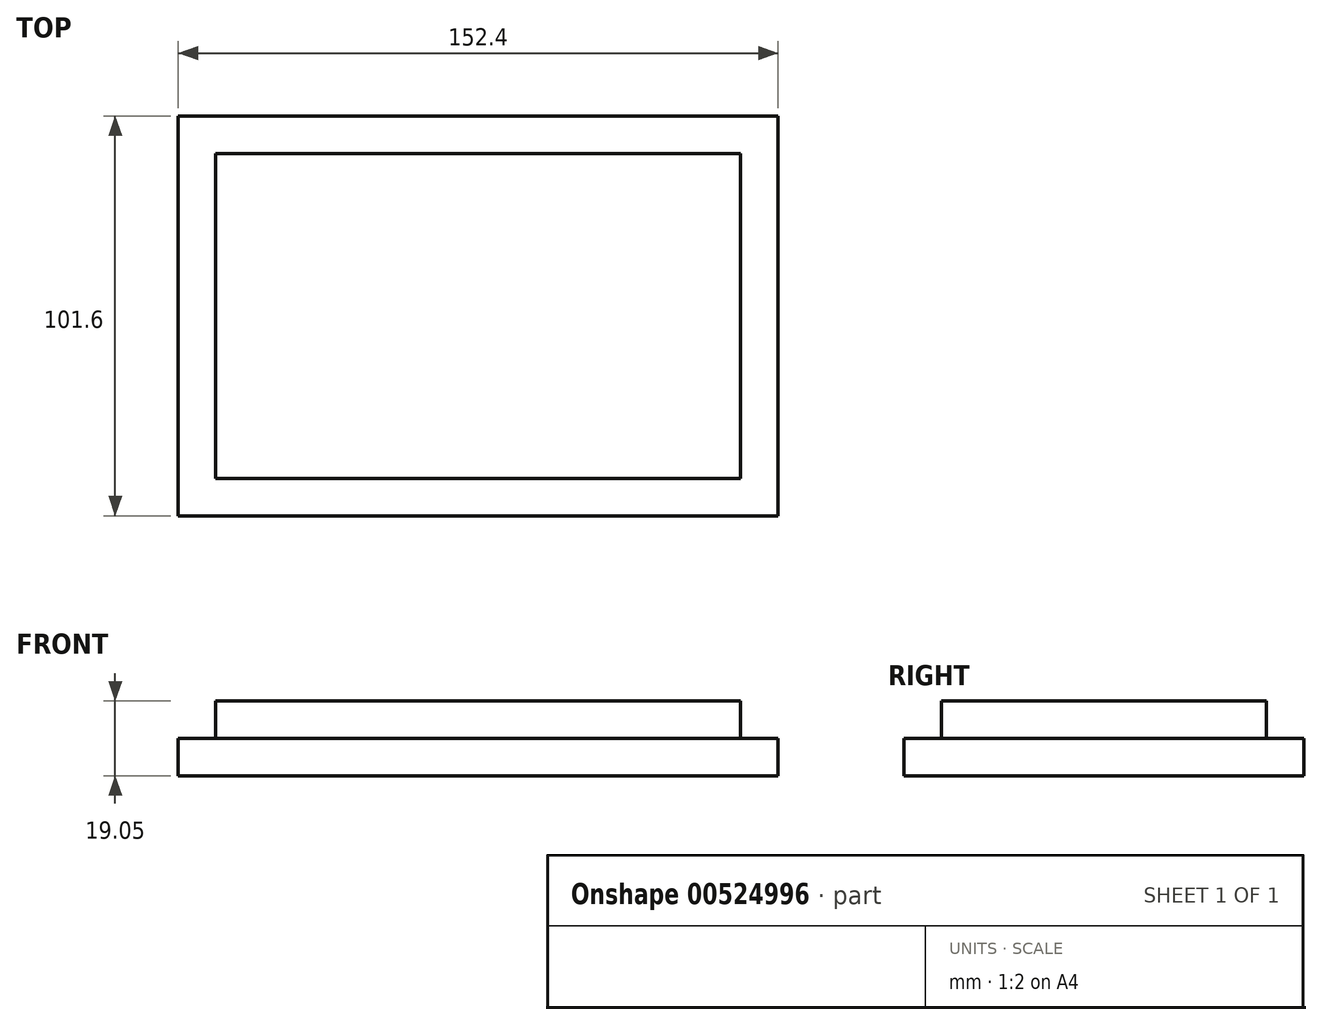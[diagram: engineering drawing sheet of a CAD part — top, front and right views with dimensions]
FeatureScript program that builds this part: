
annotation { "Feature Type Name" : "Feature", "Feature Type Description" : "" }
export const myFeature = defineFeature(function(context is Context, id is Id, definition is map)
    precondition{}
    {
        {
            var Q0;
            Q0=qCreatedBy(makeId("Top.planeOp"),FACE);
            var sketch = newSketch(context, id + "F0", { "sketchPlane" : qUnion([Q0])});
            skLineSegment(sketch, "E0.bottom", {"start": v(76.2, -50.8) * mm, "end": v(-76.2, -50.8) * mm});
            skLineSegment(sketch, "E0.top", {"start": v(76.2, 50.8) * mm, "end": v(-76.2, 50.8) * mm});
            skLineSegment(sketch, "E0.left", {"start": v(76.2, -50.8) * mm, "end": v(76.2, 50.8) * mm});
            skLineSegment(sketch, "E0.right", {"start": v(-76.2, -50.8) * mm, "end": v(-76.2, 50.8) * mm});
            skPoint(sketch, "E0.middle", {"position": v(0, 0) * mm});
            skSolve(sketch);
        }
        {
            var Q0;
            Q0 = qSketchRegion(id + "F0", true);
            extrude(context, id + "F1", {"entities" : qUnion([Q0]), "depth" : 9.52 * mm, "offsetDistance" : 25.4 * mm});
        }
        {
            var Q0;
            Q0=makeQuery(id+"F1.opExtrude","CAP_FACE",FACE,{"disambiguationData":[OSD([sQuery(id+"F0.wireOp",EDGE,"E0.bottom"),sQuery(id+"F0.wireOp",EDGE,"E0.top"),sQuery(id+"F0.wireOp",EDGE,"E0.left"),sQuery(id+"F0.wireOp",EDGE,"E0.right")])],"isStart":false});
            var sketch = newSketch(context, id + "F2", { "sketchPlane" : qUnion([Q0])});
            skLineSegment(sketch, "E1.bottom", {"start": v(66.68, -41.28) * mm, "end": v(-66.68, -41.28) * mm});
            skLineSegment(sketch, "E1.top", {"start": v(66.68, 41.28) * mm, "end": v(-66.67, 41.28) * mm});
            skLineSegment(sketch, "E1.left", {"start": v(66.68, -41.28) * mm, "end": v(66.68, 41.28) * mm});
            skLineSegment(sketch, "E1.right", {"start": v(-66.67, -41.28) * mm, "end": v(-66.67, 41.28) * mm});
            skPoint(sketch, "E1.middle", {"position": v(0, 0) * mm});
            skSolve(sketch);
        }
        {
            var Q0;
            Q0 = qSketchRegion(id + "F2", true);
            extrude(context, id + "F3", {"entities" : qUnion([Q0]), "operationType" : NewBodyOperationType.ADD, "depth" : 9.52 * mm, "offsetDistance" : 25.4 * mm});
        }
    });
